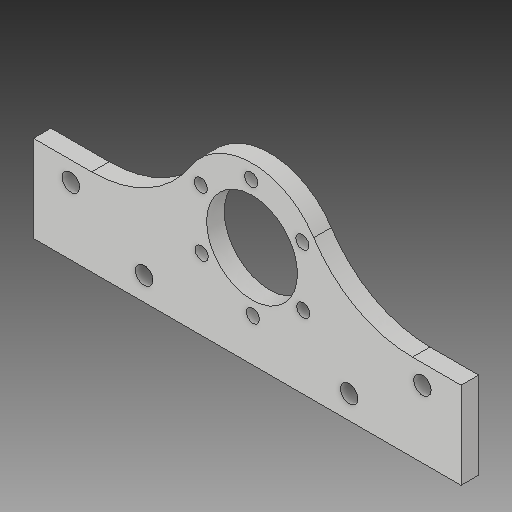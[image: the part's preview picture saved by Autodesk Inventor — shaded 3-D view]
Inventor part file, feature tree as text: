
AUTODESK INVENTOR PART (.ipt)
format: ipt  version: 2018 (Build 220112000, 112)  size: 145,920 bytes
history: native  units: mm
features: reference x13, extrude x4, sketch x4, fillet x1
ambient origin geometry x8: Origin, YZ Plane, XZ Plane, XY Plane, X Axis, Y Axis, Z Axis, Center Point
bodies: Solid1 (feature_tree)
feature tree (22):
  extrude  "Extrusion1"  Depth=6.0mm TaperAngle=0.0deg
  extrude  "Extrusion2"  Depth=6.0mm
  extrude  "Extrusion3"  Depth=60.0mm
  extrude  "Extrusion4"  Depth=40.0mm
  fillet  "Fillet2"  Radius=35.0mm
  sketch  "Sketch1"  dims[d0=34.0mm d1=6.0mm d2=0.0mm]
  reference  "Reference1"
  reference  "Reference2"
  reference  "Reference3"
  sketch  "Sketch2"  dims[d3=6.0mm d4=6.0mm]
  sketch  "Sketch3"  dims[d6=15.0mm d7=60.0mm]
  reference  "Reference5"
  reference  "Reference6"
  reference  "Reference7"
  reference  "Reference8"
  reference  "Reference9"
  reference  "Reference10"
  reference  "Reference11"
  sketch  "Sketch5"  dims[d8=6.0mm d9=0.0mm d10=8.0mm d11=35.0mm d12=6.0mm d13=0.0mm d14=0.5mm d16=6.0mm d17=0.0mm d18=40.0mm]
  reference  "Reference12"
  reference  "Reference13"
  reference  "Reference14"
